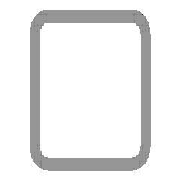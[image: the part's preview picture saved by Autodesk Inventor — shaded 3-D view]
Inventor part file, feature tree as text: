
AUTODESK INVENTOR PART (.ipt)
format: ipt  version: 2025 (Build 290162010, 162A)  size: 133,120 bytes
history: native  units: mm (DEFAULTED — no unit token found)
features: other x4, sketch x1, plane x1
ambient origin geometry x8: Origin, YZ Plane, XZ Plane, XY Plane, X Axis, Y Axis, Z Axis, Center Point
bodies: Solid1 (feature_tree), Body (feature_tree)
feature tree (6):
  parser-record x1  (decoder bookkeeping rows leaked as tree rows — omitted from the tree; the rows remain in map.json)
  other  "Driven Length"
  other  "Start Plane"
  other  "End Plane"
  sketch  "Sketch3"  dims[d3=456.986319mm d4=0.0mm d7=6.0mm d9=50.0mm d11=50.0mm d12=3.0mm d13=-0.0mm d14=456.986319mm d15=25.0mm d16=25.0mm d17=90.0deg d18=456.986319mm]
  plane  "Work Plane3"
